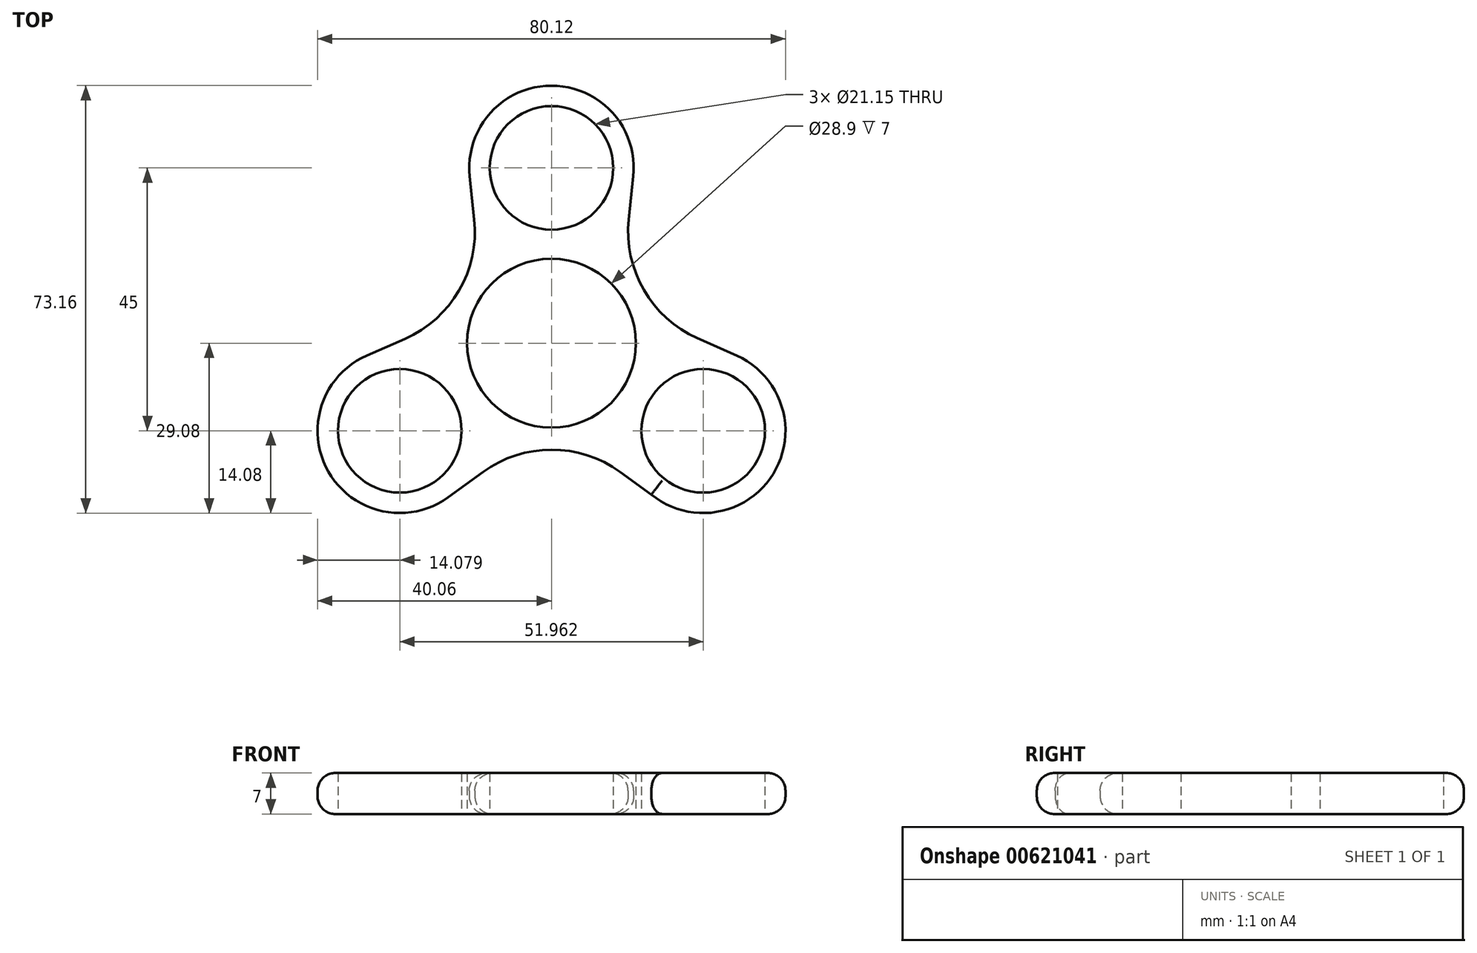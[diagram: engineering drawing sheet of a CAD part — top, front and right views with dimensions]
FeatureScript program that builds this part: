
annotation { "Feature Type Name" : "Feature", "Feature Type Description" : "" }
export const myFeature = defineFeature(function(context is Context, id is Id, definition is map)
    precondition{}
    {
        {
            var Q0;
            Q0=qCreatedBy(makeId("Top.planeOp"),FACE);
            var sketch = newSketch(context, id + "F0", { "sketchPlane" : qUnion([Q0])});
            skCircle(sketch, "E0", {"center": v(0, 0) * mm, "radius": 10.95 * mm});
            skCircle(sketch, "E1.0", {"center": v(0, 0) * mm, "radius": 14.45 * mm});
            skCircle(sketch, "E2", {"center": v(0, 30) * mm, "radius": 10.57 * mm});
            skCircle(sketch, "E3.0", {"center": v(0, 30) * mm, "radius": 14.07 * mm});
            skLineSegment(sketch, "E4", {"start": v(14, 28.53) * mm, "end": v(13.23, 21.2) * mm});
            skLineSegment(sketch, "E5", {"start": v(-14, 28.53) * mm, "end": v(-13.23, 21.16) * mm});
            skCircle(sketch, "E6", {"center": v(25.98, -15) * mm, "radius": 10.57 * mm});
            skLineSegment(sketch, "E7", {"start": v(0, 0) * mm, "end": v(25.98, -15) * mm, "construction": true});
            skLineSegment(sketch, "E8", {"start": v(0, 0) * mm, "end": v(-40.64, -23.46) * mm, "construction": true});
            skCircle(sketch, "E9", {"center": v(-25.98, -15) * mm, "radius": 10.57 * mm});
            skCircle(sketch, "E10.0", {"center": v(-25.98, -15) * mm, "radius": 14.07 * mm});
            skCircle(sketch, "E11.0", {"center": v(25.98, -15) * mm, "radius": 14.07 * mm});
            skLineSegment(sketch, "E12.0", {"start": v(0, -5.77) * mm, "end": v(23.48, -19.33) * mm});
            skLineSegment(sketch, "E12.1", {"start": v(0, -5.77) * mm, "end": v(-38.14, -27.8) * mm});
            skLineSegment(sketch, "E13", {"start": v(-31.62, -2.1) * mm, "end": v(-25.1, 0.75) * mm});
            skLineSegment(sketch, "E14", {"start": v(-17.7, -26.39) * mm, "end": v(-11.75, -22.06) * mm});
            skLineSegment(sketch, "E15", {"start": v(17.1, -25.92) * mm, "end": v(11.75, -22.04) * mm});
            skPoint(sketch, "E16.endSnap0", {"position": v(18.56, 3.69) * mm});
            skLineSegment(sketch, "E17", {"start": v(24.98, 0.86) * mm, "end": v(31.71, -2.14) * mm});
            skPoint(sketch, "E18.newPointB", {"position": v(-11, 0) * mm});
            skArc(sketch, "E18.filletArc", {"start": v(-25.1, 0.75) * mm, "mid": v(-15.83, 9.01) * mm, "end": v(-13.23, 21.16) * mm});
            skPoint(sketch, "E19.newPointB", {"position": v(11, 0) * mm});
            skArc(sketch, "E19.filletArc", {"start": v(13.23, 21.2) * mm, "mid": v(15.8, 9.12) * mm, "end": v(24.98, 0.86) * mm});
            skPoint(sketch, "E20.newPointA", {"position": v(-5.96, -9.2) * mm});
            skPoint(sketch, "E20.newPointB", {"position": v(5.94, -9.2) * mm});
            skArc(sketch, "E20.filletArc", {"start": v(11.75, -22.04) * mm, "mid": v(0, -18.23) * mm, "end": v(-11.75, -22.06) * mm});
            skSolve(sketch);
        }
        {
            var Q0;
            Q0=qSketchRegion(id+"F0",true);
            var Q1;
            {var subQ3=sQuery(id+"F0.wireOp",EDGE,"E12.1");var subQ5=sQuery(id+"F0.wireOp",EDGE,"E15");var subQ6=makeQuery(id+"F0.imprint","INTERSECT",VERTEX,{"derivedFrom":[subQ3,subQ5]});Q1=makeQuery(id+"F0.imprint","IMPRINT",FACE,{"disambiguationData":[TD([[makeQuery(id+"F0.imprint","IMPRINT",EDGE,{"disambiguationData":[TD([[subQ6,1.0]])],"derivedFrom":subQ3}),1.0]])]});}
            extrude(context, id + "F1", {"entities" : qUnion([Q0, Q1]), "depth" : 7 * mm, "offsetDistance" : 25 * mm});
        }
        {
            var Q0;
            Q0=makeQuery(id+"F1.opExtrude","CAP_EDGE",EDGE,{"disambiguationData":[OSD([sQuery(id+"F0.wireOp",EDGE,"E10.0")])],"isStart":false});
            var Q1;
            Q1=makeQuery(id+"F1.opExtrude","CAP_EDGE",EDGE,{"disambiguationData":[OSD([sQuery(id+"F0.wireOp",EDGE,"E20.filletArc")])],"isStart":true});
            fillet(context, id + "F2", {"entities" : qUnion([Q0, Q1]), "radius" : 3 * mm, "tangentPropagation" : true, "allowEdgeOverflow" : false});
        }
    });
